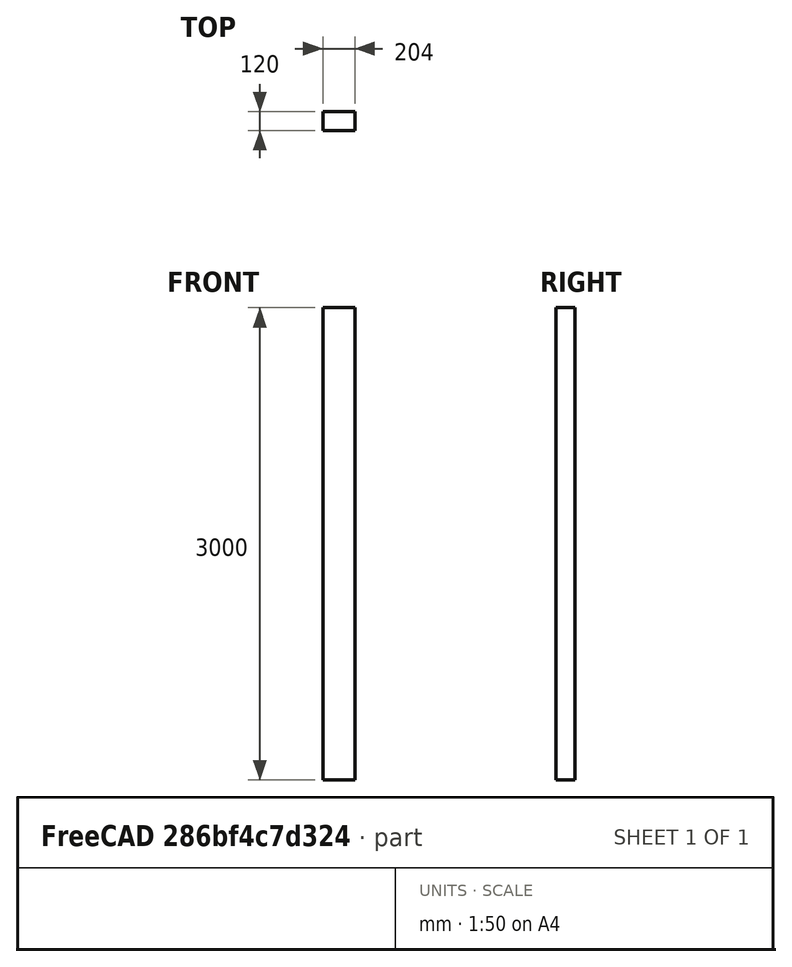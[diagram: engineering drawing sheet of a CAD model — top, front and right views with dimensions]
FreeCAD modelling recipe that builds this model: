
FCSTD DOCUMENT  (FreeCAD 0.21R33771 (Git))
Label: PQ4_vacuum
License: All rights reserved
LicenseURL: https://en.wikipedia.org/wiki/All_rights_reserved
objects: Sketcher::SketchObject×1, PartDesign::Pad×1, PartDesign::Body×1
note: 4 computed .brp shape members not serialized (recipe doc carries the construction recipe); baked Part::Feature solids carry a one-line shape summary decoded from their .brp

FEATURE [Sketcher::SketchObject] Sketch
  FullyConstrained = true
  MapMode = 5
  Support = -> [XY_Plane]
  sketch-geometry (5):
    g0: LineSegment StartX=-101.999 StartY=-59.9995 StartZ=0 EndX=-101.999 EndY=59.9995 EndZ=0
    g1: LineSegment StartX=-101.999 StartY=59.9995 StartZ=0 EndX=101.999 EndY=59.9995 EndZ=0
    g2: LineSegment StartX=101.999 StartY=59.9995 StartZ=0 EndX=101.999 EndY=-59.9995 EndZ=0
    g3: LineSegment StartX=101.999 StartY=-59.9995 StartZ=0 EndX=-101.999 EndY=-59.9995 EndZ=0
    g4: GeomPoint X=0 Y=0 Z=0
  constraints (12):
    c: Coincident(g0,g1)
    c: Coincident(g1,g2)
    c: Coincident(g2,g3)
    c: Coincident(g3,g0)
    c: Horizontal(g1)
    c: Horizontal(g3)
    c: Vertical(g0)
    c: Vertical(g2)
    c: Symmetric(g1,g0,g4)
    c: Coincident(g4,g-1)
    c: DistanceX(g1,g1) = 203.999
    c: DistanceY(g2,g2) = 119.999
FEATURE [PartDesign::Pad] Pad
  Direction = (0,0,1)
  Length = 3000
  Length2 = 10
  Midplane = true
  Profile = -> Sketch
  ReferenceAxis = -> Sketch [N_Axis]
  Type = 0
FEATURE [PartDesign::Body] Body
  Group = -> [Sketch,Pad]
  Origin = -> Origin
  Tip = -> Pad
